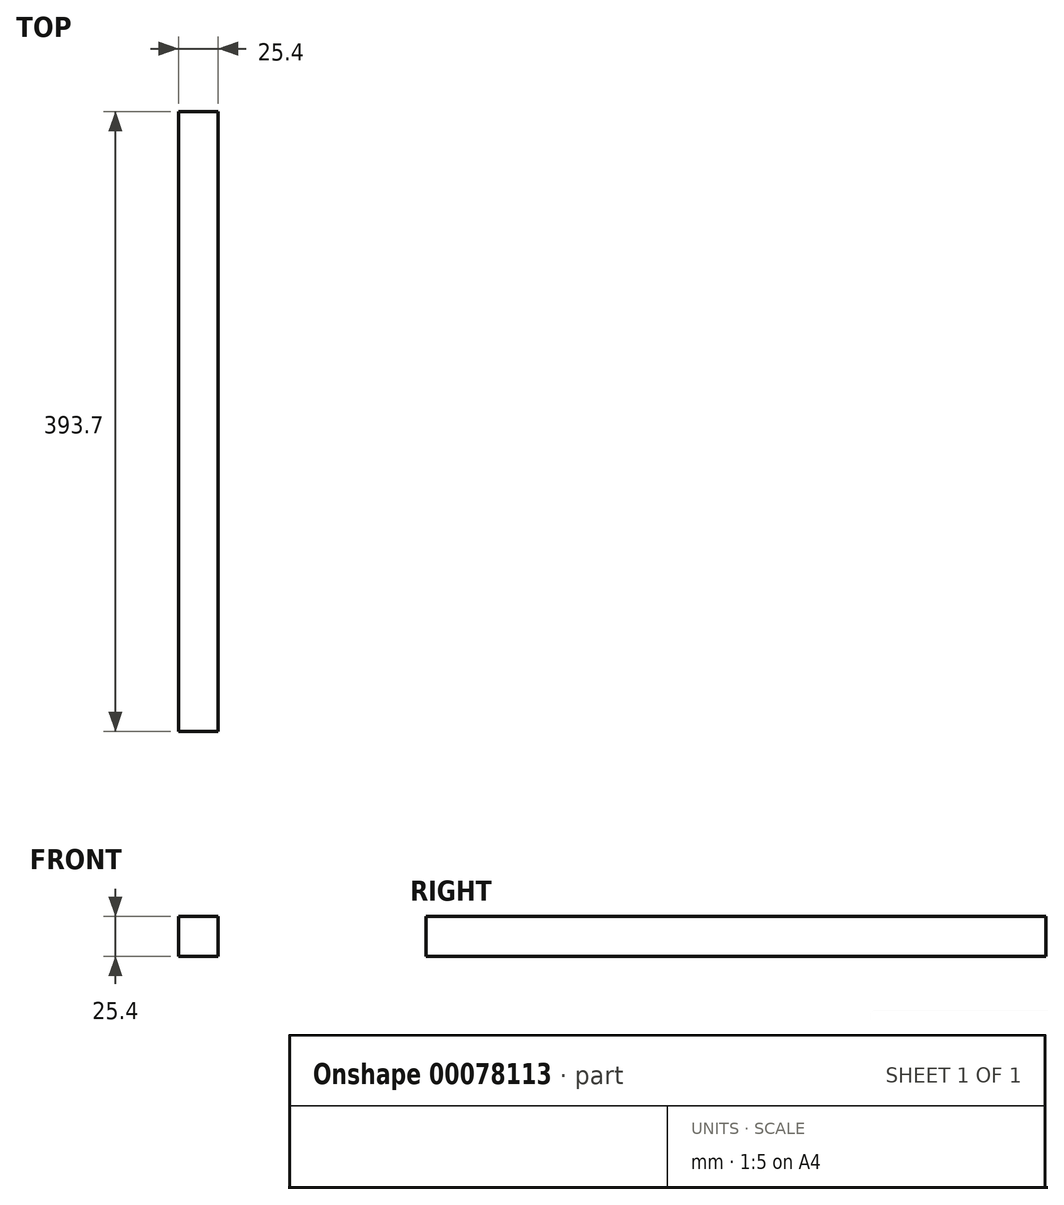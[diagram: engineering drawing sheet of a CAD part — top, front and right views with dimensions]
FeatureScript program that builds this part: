
annotation { "Feature Type Name" : "Feature", "Feature Type Description" : "" }
export const myFeature = defineFeature(function(context is Context, id is Id, definition is map)
    precondition{}
    {
        {
            var Q0;
            Q0=qCreatedBy(makeId("Front.planeOp"),FACE);
            var sketch = newSketch(context, id + "F0", { "sketchPlane" : qUnion([Q0])});
            skLineSegment(sketch, "E0.bottom", {"start": v(-29.67, 34.97) * mm, "end": v(-4.27, 34.97) * mm});
            skLineSegment(sketch, "E0.top", {"start": v(-29.67, 9.57) * mm, "end": v(-4.27, 9.57) * mm});
            skLineSegment(sketch, "E0.left", {"start": v(-29.67, 34.97) * mm, "end": v(-29.67, 9.57) * mm});
            skLineSegment(sketch, "E0.right", {"start": v(-4.27, 34.97) * mm, "end": v(-4.27, 9.57) * mm});
            skSolve(sketch);
        }
        {
            var Q0;
            Q0=makeQuery(id+"F0.imprint","IMPRINT",FACE,{"disambiguationData":[TD([[makeQuery(id+"F0.imprint","IMPRINT",EDGE,{"derivedFrom":sQuery(id+"F0.wireOp",EDGE,"E0.bottom")}),-1.0]])]});
            extrude(context, id + "F1", {"entities" : qUnion([Q0]), "depth" : 393.7 * mm});
        }
    });
